# Revit family: Plumbing Fixture-Grease_Interseptor_Mifab_XL-MI-G
name_source: partatom
category: Plumbing Fixtures
revit_build: Autodesk Revit Structure 2013 (Build: 20120221_2030(x64)
units: mm (PartAtom-declared; Revit-internal decimal feet)

## types (12) — shared parameters
Assembly Code = D2090300
Description = Large Capacity Grease Interceptor
Interceptor Material = Acid Resistant Epoxy Coated Green
Manufacturer = MIFAB
URL = www.mifab.com
zero-valued in all types: Default Elevation, WFU

## per-type parameters (varying)
| type | A | B | C | D | E | F | Flow Rate | Grease Capacity | Standard Inlet And Outlet Radii | Water Capacity |
| XL-MI-G-0 | 42 " | 28 " | 6 " | 26 " | 32 " | 4 " | 75 GPM | 150 lbs | 2 " | 108.05 Gallons |
| XL-MI-G-1 | 55 " | 37 " | 8 " | 26 " | 34 " | 4 " | 100 GPM | 200 lbs | 2 " | 192.73 Gallons |
| XL-MI-G-2 | 58 " | 38 " | 8 " | 28 " | 36 " | 4 " | 125 GPM | 250 lbs | 2 " | 226.91 Gallons |
| XL-MI-G-3 | 61 " | 39 " | 8 " | 30 " | 38 " | 4 " | 150 GPM | 300 lbs | 2 " | 264.61 Gallons |
| XL-MI-G-4 | 70 " | 44 " | 10 " | 34 " | 44 " | 4 " | 200 GPM | 400 lbs | 2 " | 395.64 Gallons |
| XL-MI-G-5 | 75 " | 46 " | 10 " | 38 " | 48 " | 4 " | 250 GPM | 500 lbs | 2 " | 501.00 Gallons |
| XL-MI-G-6 | 77 " | 49 " | 12 " | 40 " | 52 " | 4 " | 300 GPM | 600 lbs | 2 " | 579.87 Gallons |
| XL-MI-G-7 | 80 " | 51 " | 12 " | 40 " | 52 " | 6 " | 350 GPM | 700 lbs | 3 " | 612.18 Gallons |
| XL-MI-G-8 | 84 " | 56 " | 14 " | 44 " | 58 " | 6 " | 400 GPM | 800 lbs | 3 " | 805.09 Gallons |
| XL-MI-G-9 | 92 " | 61 " | 14 " | 54 " | 68 " | 6 " | 500 GPM | 1000 lbs | 3 " | 1172.34 Gallons |
| XL-MI-G-10 | 102 " | 74 " | 14 " | 62 " | 76 " | 8 " | 600 GPM | 1200 lbs | 4 " | 1807.79 Gallons |
| XL-MI-G-11 | 108 " | 76 " | 14 " | 66 " | 80 " | 8 " | 750 GPM | 1500 lbs | 4 " | 2580.71 Gallons |

note: column(s) folded — value = type name in every type: Model

## geometry (parser evidence)
native form markers: Blend x5, Sweep x1
no freeform markers — native parametric forms only
